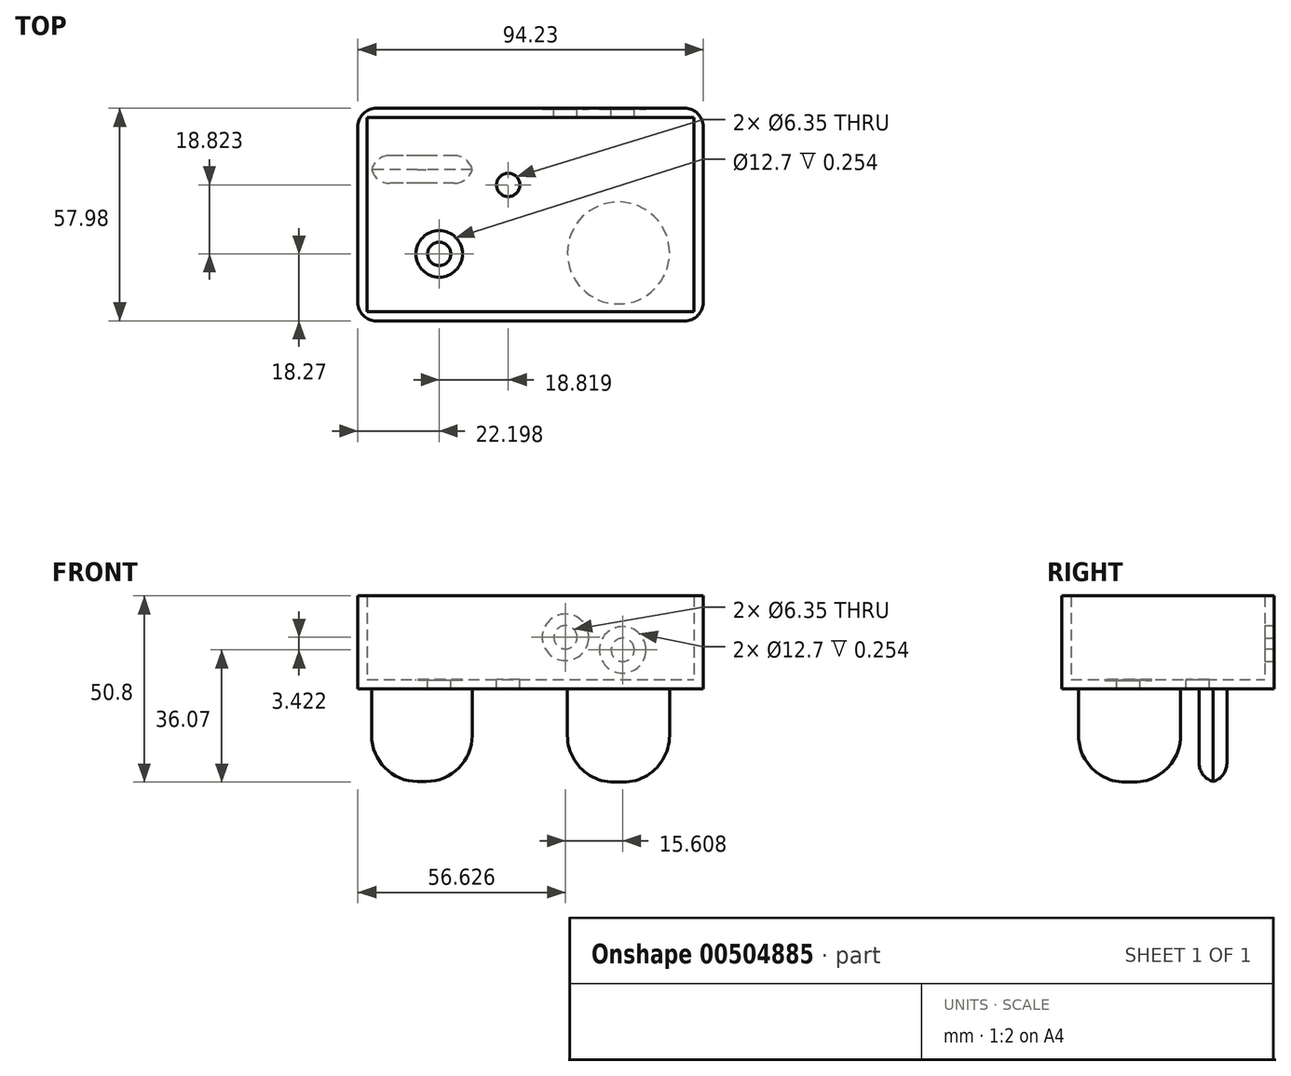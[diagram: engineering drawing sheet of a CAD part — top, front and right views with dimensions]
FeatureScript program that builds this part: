
annotation { "Feature Type Name" : "Feature", "Feature Type Description" : "" }
export const myFeature = defineFeature(function(context is Context, id is Id, definition is map)
    precondition{}
    {
        {
            var Q0;
            Q0=qCreatedBy(makeId("Top.planeOp"),FACE);
            var sketch = newSketch(context, id + "F0", { "sketchPlane" : qUnion([Q0])});
            skLineSegment(sketch, "E0.bottom", {"start": v(-85.26, -25.56) * mm, "end": v(8.97, -25.56) * mm});
            skLineSegment(sketch, "E0.top", {"start": v(-85.26, 32.42) * mm, "end": v(8.97, 32.42) * mm});
            skLineSegment(sketch, "E0.left", {"start": v(-85.26, -25.56) * mm, "end": v(-85.26, 32.42) * mm});
            skLineSegment(sketch, "E0.right", {"start": v(8.97, -25.56) * mm, "end": v(8.97, 32.42) * mm});
            skSolve(sketch);
        }
        {
            var Q0;
            Q0=makeQuery(id+"F0.imprint","IMPRINT",FACE,{"disambiguationData":[TD([[makeQuery(id+"F0.imprint","IMPRINT",EDGE,{"derivedFrom":sQuery(id+"F0.wireOp",EDGE,"E0.bottom")}),1.0]])]});
            extrude(context, id + "F1", {"entities" : qUnion([Q0]), "depth" : 25.4 * mm});
        }
        {
            var Q0;
            Q0=makeQuery(id+"F1.opExtrude","CAP_FACE",FACE,{"disambiguationData":[OSD([sQuery(id+"F0.wireOp",EDGE,"E0.bottom"),sQuery(id+"F0.wireOp",EDGE,"E0.top"),sQuery(id+"F0.wireOp",EDGE,"E0.left"),sQuery(id+"F0.wireOp",EDGE,"E0.right")])],"isStart":false});
            shell(context, id + "F2", {"entities" : qUnion([Q0]), "thickness" : 2.54 * mm});
        }
        {
            var Q0;
            Q0=makeQuery(id+"F1.opExtrude","SWEPT_EDGE",EDGE,{"disambiguationData":[OSD([sQuery(id+"F0.wireOp",EDGE,"E0.bottom"),sQuery(id+"F0.wireOp",EDGE,"E0.left")])]});
            var Q1;
            Q1=makeQuery(id+"F1.opExtrude","SWEPT_EDGE",EDGE,{"disambiguationData":[OSD([sQuery(id+"F0.wireOp",EDGE,"E0.bottom"),sQuery(id+"F0.wireOp",EDGE,"E0.right")])]});
            var Q2;
            Q2=makeQuery(id+"F1.opExtrude","SWEPT_EDGE",EDGE,{"disambiguationData":[OSD([sQuery(id+"F0.wireOp",EDGE,"E0.top"),sQuery(id+"F0.wireOp",EDGE,"E0.right")])]});
            var Q3;
            Q3=makeQuery(id+"F1.opExtrude","SWEPT_EDGE",EDGE,{"disambiguationData":[OSD([sQuery(id+"F0.wireOp",EDGE,"E0.top"),sQuery(id+"F0.wireOp",EDGE,"E0.left")])]});
            fillet(context, id + "F3", {"entities" : qUnion([Q0, Q1, Q2, Q3]), "radius" : 5.08 * mm, "tangentPropagation" : true, "allowEdgeOverflow" : false});
        }
        {
            var Q0;
            Q0=makeQuery(id+"F2.opShell","OFFSET_FACE",FACE,{"disambiguationData":[OSD([sQuery(id+"F0.wireOp",EDGE,"E0.bottom"),sQuery(id+"F0.wireOp",EDGE,"E0.top"),sQuery(id+"F0.wireOp",EDGE,"E0.left"),sQuery(id+"F0.wireOp",EDGE,"E0.right")])]});
            var sketch = newSketch(context, id + "F4", { "sketchPlane" : qUnion([Q0])});
            skCircle(sketch, "E1", {"center": v(-44.24, 11.53) * mm, "radius": 6.15 * mm});
            skSolve(sketch);
        }
        {
            var Q0;
            Q0=sQuery(id+"F4.wireOp",VERTEX,"E1.center");
            var Q1;
            Q1=makeQuery(id+"F1.opExtrude","SWEPT_BODY",BODY,{"disambiguationData":[OSD([sQuery(id+"F0.wireOp",EDGE,"E0.bottom"),sQuery(id+"F0.wireOp",EDGE,"E0.top"),sQuery(id+"F0.wireOp",EDGE,"E0.left"),sQuery(id+"F0.wireOp",EDGE,"E0.right")])]});
            hole(context, id + "F5", {"style" : HoleStyle.SIMPLE, "endStyle" : HoleEndStyle.THROUGH, "holeDiameter" : 6.35 * mm, "isTappedThrough" : true, "tappedDepth" : 12.7 * mm, "tapClearance" : 3, "locations" : qUnion([Q0]), "scope" : qUnion([Q1])});
        }
        {
            var Q0;
            Q0=makeQuery(id+"F2.opShell","OFFSET_FACE",FACE,{"disambiguationData":[OSD([sQuery(id+"F0.wireOp",EDGE,"E0.bottom"),sQuery(id+"F0.wireOp",EDGE,"E0.top"),sQuery(id+"F0.wireOp",EDGE,"E0.left"),sQuery(id+"F0.wireOp",EDGE,"E0.right")])]});
            var sketch = newSketch(context, id + "F6", { "sketchPlane" : qUnion([Q0])});
            skCircle(sketch, "E2", {"center": v(-63.06, -7.29) * mm, "radius": 8.72 * mm});
            skSolve(sketch);
        }
        {
            var Q0;
            Q0=sQuery(id+"F6.wireOp",VERTEX,"E2.center");
            var Q1;
            Q1=makeQuery(id+"F1.opExtrude","SWEPT_BODY",BODY,{"disambiguationData":[OSD([sQuery(id+"F0.wireOp",EDGE,"E0.bottom"),sQuery(id+"F0.wireOp",EDGE,"E0.top"),sQuery(id+"F0.wireOp",EDGE,"E0.left"),sQuery(id+"F0.wireOp",EDGE,"E0.right")])]});
            hole(context, id + "F7", {"style" : HoleStyle.C_BORE, "endStyle" : HoleEndStyle.BLIND, "holeDiameter" : 6.35 * mm, "cBoreDiameter" : 12.7 * mm, "cBoreDepth" : 0.25 * mm, "holeDepth" : 12.7 * mm, "isTappedThrough" : true, "tappedDepth" : 12.7 * mm, "tapClearance" : 3, "locations" : qUnion([Q0]), "scope" : qUnion([Q1])});
        }
        {
            var Q0;
            Q0=makeQuery(id+"F1.opExtrude","SWEPT_FACE",FACE,{"disambiguationData":[OSD([sQuery(id+"F0.wireOp",EDGE,"E0.top")])]});
            var sketch = newSketch(context, id + "F8", { "sketchPlane" : qUnion([Q0])});
            skLineSegment(sketch, "E3.bottom", {"start": v(13.03, 14.1) * mm, "end": v(28.63, 14.1) * mm});
            skLineSegment(sketch, "E3.top", {"start": v(13.03, 10.67) * mm, "end": v(28.63, 10.67) * mm});
            skLineSegment(sketch, "E3.left", {"start": v(13.03, 14.1) * mm, "end": v(13.03, 10.67) * mm});
            skLineSegment(sketch, "E3.right", {"start": v(28.63, 14.1) * mm, "end": v(28.63, 10.67) * mm});
            skSolve(sketch);
        }
        {
            var Q0;
            Q0=sQuery(id+"F8.wireOp",VERTEX,"E3.left.end");
            var Q1;
            Q1=sQuery(id+"F8.wireOp",VERTEX,"E3.right.start");
            var Q2;
            Q2=makeQuery(id+"F1.opExtrude","SWEPT_BODY",BODY,{"disambiguationData":[OSD([sQuery(id+"F0.wireOp",EDGE,"E0.bottom"),sQuery(id+"F0.wireOp",EDGE,"E0.top"),sQuery(id+"F0.wireOp",EDGE,"E0.left"),sQuery(id+"F0.wireOp",EDGE,"E0.right")])]});
            hole(context, id + "F9", {"style" : HoleStyle.C_BORE, "endStyle" : HoleEndStyle.BLIND, "holeDiameter" : 6.35 * mm, "cBoreDiameter" : 12.7 * mm, "cBoreDepth" : 0.25 * mm, "holeDepth" : 12.7 * mm, "isTappedThrough" : true, "tappedDepth" : 12.7 * mm, "tapClearance" : 3, "locations" : qUnion([Q0, Q1]), "scope" : qUnion([Q2])});
        }
        {
            var Q0;
            Q0=makeQuery(id+"F1.opExtrude","CAP_FACE",FACE,{"disambiguationData":[OSD([sQuery(id+"F0.wireOp",EDGE,"E0.bottom"),sQuery(id+"F0.wireOp",EDGE,"E0.top"),sQuery(id+"F0.wireOp",EDGE,"E0.left"),sQuery(id+"F0.wireOp",EDGE,"E0.right")])],"isStart":true});
            var sketch = newSketch(context, id + "F10", { "sketchPlane" : qUnion([Q0])});
            skCircle(sketch, "E4", {"center": v(-14.17, 7.03) * mm, "radius": 13.92 * mm});
            skSolve(sketch);
        }
        {
            var Q0;
            Q0 = qSketchRegion(id + "F10", true);
            extrude(context, id + "F11", {"entities" : qUnion([Q0]), "operationType" : NewBodyOperationType.ADD, "depth" : 25.4 * mm});
        }
        {
            var Q0;
            Q0=makeQuery(id+"F11.opExtrude","CAP_EDGE",EDGE,{"disambiguationData":[OSD([sQuery(id+"F10.wireOp",EDGE,"E4")])],"isStart":false});
            fillet(context, id + "F12", {"entities" : qUnion([Q0]), "radius" : 12.7 * mm, "tangentPropagation" : true, "allowEdgeOverflow" : false});
        }
        {
            var Q0;
            Q0=makeQuery(id+"F1.opExtrude","CAP_FACE",FACE,{"disambiguationData":[OSD([sQuery(id+"F0.wireOp",EDGE,"E0.bottom"),sQuery(id+"F0.wireOp",EDGE,"E0.top"),sQuery(id+"F0.wireOp",EDGE,"E0.left"),sQuery(id+"F0.wireOp",EDGE,"E0.right")])],"isStart":true});
            var sketch = newSketch(context, id + "F13", { "sketchPlane" : qUnion([Q0])});
            skLineSegment(sketch, "E5.bottom", {"start": v(-53.9, -19.51) * mm, "end": v(-81.67, -19.51) * mm});
            skLineSegment(sketch, "E5.top", {"start": v(-53.9, -11.98) * mm, "end": v(-81.67, -11.98) * mm});
            skLineSegment(sketch, "E5.left", {"start": v(-53.9, -19.51) * mm, "end": v(-53.9, -11.98) * mm});
            skLineSegment(sketch, "E5.right", {"start": v(-81.67, -19.51) * mm, "end": v(-81.67, -11.98) * mm});
            skSolve(sketch);
        }
        {
            var Q0;
            Q0=makeQuery(id+"F13.imprint","IMPRINT",FACE,{"disambiguationData":[TD([[makeQuery(id+"F13.imprint","IMPRINT",EDGE,{"derivedFrom":sQuery(id+"F13.wireOp",EDGE,"E5.bottom")}),-1.0]])]});
            extrude(context, id + "F14", {"entities" : qUnion([Q0]), "operationType" : NewBodyOperationType.ADD, "depth" : 25.4 * mm});
        }
        {
            var Q0;
            Q0=makeQuery(id+"F14.opExtrude","CAP_EDGE",EDGE,{"disambiguationData":[OSD([sQuery(id+"F13.wireOp",EDGE,"E5.left")])],"isStart":false});
            var Q1;
            Q1=makeQuery(id+"F14.opExtrude","CAP_EDGE",EDGE,{"disambiguationData":[OSD([sQuery(id+"F13.wireOp",EDGE,"E5.right")])],"isStart":false});
            fillet(context, id + "F15", {"entities" : qUnion([Q0, Q1]), "radius" : 12.7 * mm, "tangentPropagation" : true, "allowEdgeOverflow" : false});
        }
        {
            var Q0;
            Q0=makeQuery(id+"F15.opFillet","BLEND_EDGE",EDGE,{"blendedFrom":[makeQuery(id+"F14.opExtrude","CAP_EDGE",EDGE,{"disambiguationData":[OSD([sQuery(id+"F13.wireOp",EDGE,"E5.right")])],"isStart":false}),makeQuery(id+"F14.opExtrude","SWEPT_FACE",FACE,{"disambiguationData":[OSD([sQuery(id+"F13.wireOp",EDGE,"E5.top")])]})],"blendedInto":[makeQuery(id+"F14.opExtrude","SWEPT_FACE",FACE,{"disambiguationData":[OSD([sQuery(id+"F13.wireOp",EDGE,"E5.top")])]})]});
            var Q1;
            Q1=makeQuery(id+"F15.opFillet","BLEND_EDGE",EDGE,{"blendedFrom":[makeQuery(id+"F14.opExtrude","CAP_EDGE",EDGE,{"disambiguationData":[OSD([sQuery(id+"F13.wireOp",EDGE,"E5.left")])],"isStart":false}),makeQuery(id+"F14.opExtrude","SWEPT_FACE",FACE,{"disambiguationData":[OSD([sQuery(id+"F13.wireOp",EDGE,"E5.bottom")])]})],"blendedInto":[makeQuery(id+"F14.opExtrude","SWEPT_FACE",FACE,{"disambiguationData":[OSD([sQuery(id+"F13.wireOp",EDGE,"E5.bottom")])]})]});
            fillet(context, id + "F16", {"entities" : qUnion([Q0, Q1]), "radius" : 5.08 * mm, "tangentPropagation" : true, "allowEdgeOverflow" : false});
        }
    });
